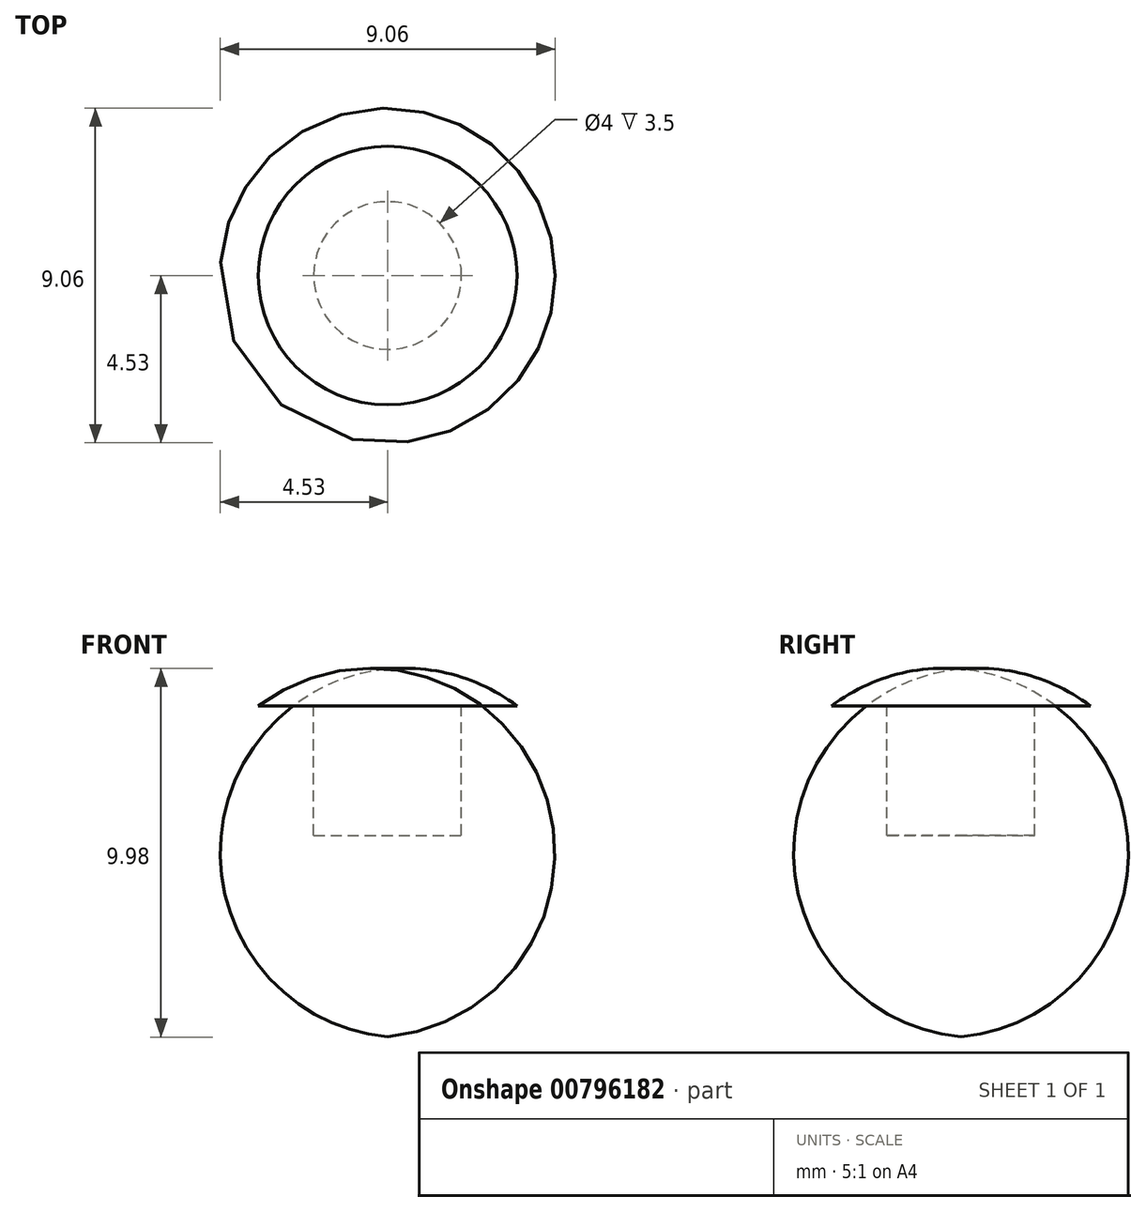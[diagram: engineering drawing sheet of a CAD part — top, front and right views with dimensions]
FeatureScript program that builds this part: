
annotation { "Feature Type Name" : "Feature", "Feature Type Description" : "" }
export const myFeature = defineFeature(function(context is Context, id is Id, definition is map)
    precondition{}
    {
        {
            var Q0;
            Q0=qCreatedBy(makeId("Front.planeOp"),FACE);
            var sketch = newSketch(context, id + "F0", { "sketchPlane" : qUnion([Q0])});
            skLineSegment(sketch, "E0", {"start": v(0, 0) * mm, "end": v(3.5, 0) * mm});
            skLineSegment(sketch, "E1", {"start": v(0, 0) * mm, "end": v(0, 1) * mm});
            skArc(sketch, "E2", {"start": v(3.5, 0) * mm, "mid": v(1.84, 0.83) * mm, "end": v(0, 1) * mm});
            skSolve(sketch);
        }
        {
            var Q0;
            Q0=makeQuery(id+"F0.imprint","IMPRINT",FACE,{"disambiguationData":[TD([[makeQuery(id+"F0.imprint","IMPRINT",EDGE,{"derivedFrom":sQuery(id+"F0.wireOp",EDGE,"E0")}),1.0]])]});
            var Q1;
            Q1=sQuery(id+"F0.wireOp",EDGE,"E1");
            revolve(context, id + "F1", {"surfaceOperationType" : NewSurfaceOperationType.NEW, "entities" : qUnion([Q0]), "axis" : qUnion([Q1]), "revolveType" : RevolveType.FULL});
        }
        {
            var Q0;
            Q0=makeQuery(id+"F1.opRevolve","SWEPT_FACE",FACE,{"disambiguationData":[OSD([sQuery(id+"F0.wireOp",EDGE,"E0")])]});
            var sketch = newSketch(context, id + "F2", { "sketchPlane" : qUnion([Q0])});
            skCircle(sketch, "E3", {"center": v(0, 0) * mm, "radius": 2 * mm});
            skSolve(sketch);
        }
        {
            var Q0;
            Q0=makeQuery(id+"F2.imprint","IMPRINT",FACE,{"disambiguationData":[TD([[makeQuery(id+"F2.imprint","IMPRINT",EDGE,{"derivedFrom":sQuery(id+"F2.wireOp",EDGE,"E3")}),1.0]])]});
            extrude(context, id + "F3", {"entities" : qUnion([Q0]), "operationType" : NewBodyOperationType.ADD, "depth" : 3.5 * mm, "offsetDistance" : 25 * mm});
        }
    });
